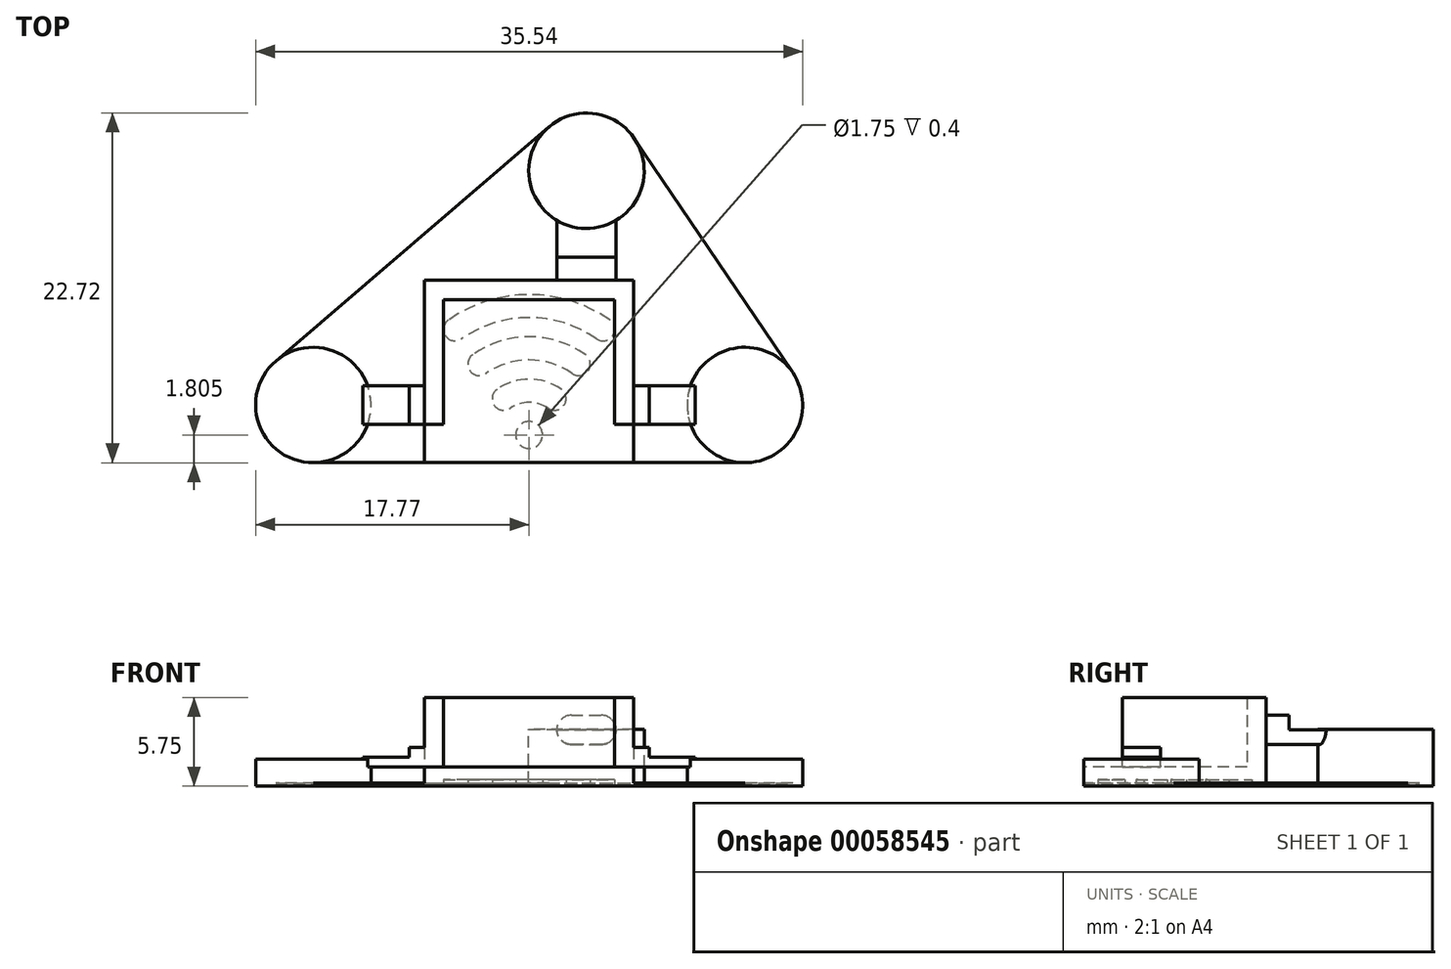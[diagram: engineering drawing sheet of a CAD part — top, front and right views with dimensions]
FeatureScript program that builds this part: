
annotation { "Feature Type Name" : "Feature", "Feature Type Description" : "" }
export const myFeature = defineFeature(function(context is Context, id is Id, definition is map)
    precondition{}
    {
        {
            var Q0;
            Q0=qCreatedBy(makeId("Top.planeOp"),FACE);
            var sketch = newSketch(context, id + "F0", { "sketchPlane" : qUnion([Q0])});
            skLineSegment(sketch, "E0.bottom", {"start": v(-6.8, 5.93) * mm, "end": v(6.8, 5.92) * mm});
            skLineSegment(sketch, "E0.top", {"start": v(-6.8, -5.92) * mm, "end": v(6.8, -5.93) * mm});
            skLineSegment(sketch, "E0.left", {"start": v(-6.8, 5.93) * mm, "end": v(-6.8, -5.93) * mm});
            skLineSegment(sketch, "E0.right", {"start": v(6.8, 5.93) * mm, "end": v(6.8, -5.93) * mm});
            skLineSegment(sketch, "E1", {"start": v(0, 11.13) * mm, "end": v(0, -11.32) * mm, "construction": true});
            skLineSegment(sketch, "E2", {"start": v(-11.98, 0) * mm, "end": v(11.2, 0) * mm, "construction": true});
            skSolve(sketch);
        }
        {
            var Q0;
            Q0 = qSketchRegion(id + "F0", true);
            extrude(context, id + "F1", {"entities" : qUnion([Q0]), "depth" : 5.75 * mm});
        }
        {
            var Q0;
            Q0=makeQuery(id+"F1.opExtrude","CAP_FACE",FACE,{"disambiguationData":[OSD([sQuery(id+"F0.wireOp",EDGE,"E0.bottom"),sQuery(id+"F0.wireOp",EDGE,"E0.top"),sQuery(id+"F0.wireOp",EDGE,"E0.left"),sQuery(id+"F0.wireOp",EDGE,"E0.right")])],"isStart":false});
            shell(context, id + "F2", {"entities" : qUnion([Q0]), "thickness" : 1.25 * mm});
        }
        {
            var Q0;
            Q0=makeQuery(id+"F1.opExtrude","SWEPT_FACE",FACE,{"disambiguationData":[OSD([sQuery(id+"F0.wireOp",EDGE,"E0.right")])]});
            var sketch = newSketch(context, id + "F3", { "sketchPlane" : qUnion([Q0])});
            skLineSegment(sketch, "E3.bottom", {"start": v(-0.93, 2.5) * mm, "end": v(-3.43, 2.5) * mm});
            skLineSegment(sketch, "E3.top", {"start": v(-0.93, 1.25) * mm, "end": v(-3.43, 1.25) * mm});
            skLineSegment(sketch, "E3.left", {"start": v(-0.93, 2.5) * mm, "end": v(-0.93, 1.25) * mm});
            skLineSegment(sketch, "E4", {"start": v(-3.43, 1.25) * mm, "end": v(-3.43, 2.5) * mm});
            skSolve(sketch);
        }
        {
            var Q0;
            Q0 = qSketchRegion(id + "F3", true);
            extrude(context, id + "F4", {"entities" : qUnion([Q0]), "operationType" : NewBodyOperationType.ADD, "depth" : 1 * mm});
        }
        {
            var Q0;
            Q0=makeQuery(id+"F1.opExtrude","SWEPT_BODY",BODY,{"disambiguationData":[OSD([sQuery(id+"F0.wireOp",EDGE,"E0.bottom"),sQuery(id+"F0.wireOp",EDGE,"E0.top"),sQuery(id+"F0.wireOp",EDGE,"E0.left"),sQuery(id+"F0.wireOp",EDGE,"E0.right")])]});
            var Q1;
            Q1=qCreatedBy(makeId("Right.planeOp"),FACE);
            mirror(context, id + "F5", {"operationType" : NewBodyOperationType.ADD, "entities" : qUnion([Q0]), "mirrorPlane" : qUnion([Q1])});
        }
        {
            var Q0;
            {var subQ0=makeQuery(id+"F4.boolean.opBoolean","MERGE",FACE,{"derivedFrom":[makeQuery(id+"F1.opExtrude","SWEPT_FACE",FACE,{"disambiguationData":[OSD([sQuery(id+"F0.wireOp",EDGE,"E0.top")])]}),makeQuery(id+"F4.opExtrude","SWEPT_FACE",FACE,{"disambiguationData":[OSD([sQuery(id+"F3.wireOp",EDGE,"E3.right")])]})]});Q0=makeQuery(id+"F5.boolean.opBoolean","MERGE",FACE,{"derivedFrom":[subQ0,makeQuery(id+"F5.opPattern","COPY",FACE,{"derivedFrom":subQ0,"instanceName":"1"})]});}
            var sketch = newSketch(context, id + "F6", { "sketchPlane" : qUnion([Q0])});
            skLineSegment(sketch, "E5.bottom", {"start": v(-2.5, 3.65) * mm, "end": v(2.5, 3.65) * mm});
            skLineSegment(sketch, "E5.top", {"start": v(-2.5, 2.5) * mm, "end": v(2.5, 2.5) * mm});
            skLineSegment(sketch, "E5.left", {"start": v(-2.5, 3.65) * mm, "end": v(-2.5, 2.5) * mm});
            skLineSegment(sketch, "E5.right", {"start": v(2.5, 3.65) * mm, "end": v(2.5, 2.5) * mm});
            skSolve(sketch);
        }
        {
            var Q0;
            Q0 = qSketchRegion(id + "F6", true);
            extrude(context, id + "F7", {"entities" : qUnion([Q0]), "operationType" : NewBodyOperationType.ADD, "depth" : 1.5 * mm});
        }
        {
            var Q0;
            Q0=makeQuery(id+"F1.opExtrude","SWEPT_FACE",FACE,{"disambiguationData":[OSD([sQuery(id+"F0.wireOp",EDGE,"E0.bottom")])]});
            var sketch = newSketch(context, id + "F8", { "sketchPlane" : qUnion([Q0])});
            skLineSegment(sketch, "E6.bottom", {"start": v(-2.75, 2.7) * mm, "end": v(-4.7, 2.7) * mm});
            skLineSegment(sketch, "E6.top", {"start": v(-2.75, 4.6) * mm, "end": v(-4.7, 4.6) * mm});
            skLineSegment(sketch, "E6.left", {"start": v(-1.8, 3.65) * mm, "end": v(-1.8, 3.65) * mm});
            skLineSegment(sketch, "E6.right", {"start": v(-5.65, 3.65) * mm, "end": v(-5.65, 3.65) * mm});
            skPoint(sketch, "E7.visualSharp", {"position": v(-1.8, 2.7) * mm});
            skArc(sketch, "E7.filletArc", {"start": v(-2.75, 2.7) * mm, "mid": v(-2.08, 2.98) * mm, "end": v(-1.8, 3.65) * mm});
            skPoint(sketch, "E8.visualSharp", {"position": v(-1.8, 4.6) * mm});
            skArc(sketch, "E8.filletArc", {"start": v(-1.8, 3.65) * mm, "mid": v(-2.08, 4.32) * mm, "end": v(-2.75, 4.6) * mm});
            skPoint(sketch, "E9.visualSharp", {"position": v(-5.65, 4.6) * mm});
            skArc(sketch, "E9.filletArc", {"start": v(-4.7, 4.6) * mm, "mid": v(-5.37, 4.32) * mm, "end": v(-5.65, 3.65) * mm});
            skPoint(sketch, "E10.visualSharp", {"position": v(-5.65, 2.7) * mm});
            skArc(sketch, "E10.filletArc", {"start": v(-5.65, 3.65) * mm, "mid": v(-5.37, 2.98) * mm, "end": v(-4.7, 2.7) * mm});
            skSolve(sketch);
        }
        {
            var Q0;
            Q0 = qSketchRegion(id + "F8", true);
            extrude(context, id + "F9", {"entities" : qUnion([Q0]), "operationType" : NewBodyOperationType.ADD, "depth" : 1.5 * mm});
        }
        {
            var Q0;
            Q0=qCreatedBy(makeId("Right.planeOp"),FACE);
            var sketch = newSketch(context, id + "F10", { "sketchPlane" : qUnion([Q0])});
            skLineSegment(sketch, "E11.bottom", {"start": v(-3.43, 1.25) * mm, "end": v(-7.79, 1.25) * mm});
            skLineSegment(sketch, "E11.top", {"start": v(-3.43, 5.94) * mm, "end": v(-7.79, 5.94) * mm});
            skLineSegment(sketch, "E11.left", {"start": v(-3.43, 1.25) * mm, "end": v(-3.43, 5.94) * mm});
            skLineSegment(sketch, "E11.right", {"start": v(-7.79, 1.25) * mm, "end": v(-7.79, 5.94) * mm});
            skSolve(sketch);
        }
        {
            var Q0;
            Q0 = qSketchRegion(id + "F10", true);
            extrude(context, id + "F11", {"entities" : qUnion([Q0]), "operationType" : NewBodyOperationType.REMOVE, "endBound" : BoundingType.THROUGH_ALL, "oppositeDirection" : true, "depth" : 25 * mm, "hasSecondDirection" : true, "secondDirectionBound" : SecondDirectionBoundingType.THROUGH_ALL, "secondDirectionOppositeDirection" : false, "secondDirectionDepth" : 25 * mm});
        }
        {
            var Q0;
            Q0=qCreatedBy(makeId("Top.planeOp"),FACE);
            var sketch = newSketch(context, id + "F12", { "sketchPlane" : qUnion([Q0])});
            skCircle(sketch, "E12", {"center": v(0, -4.12) * mm, "radius": 0.88 * mm});
            skLineSegment(sketch, "E13", {"start": v(0, 4.9) * mm, "end": v(0, -4.12) * mm, "construction": true});
            skLineSegment(sketch, "E14", {"start": v(0, -4.12) * mm, "end": v(-5.13, 3.2) * mm, "construction": true});
            skLineSegment(sketch, "E15", {"start": v(0, -4.12) * mm, "end": v(5.18, 3.28) * mm, "construction": true});
            skArc(sketch, "E16", {"start": v(1.65, -1.77) * mm, "mid": v(0, -1.25) * mm, "end": v(-1.65, -1.77) * mm});
            skArc(sketch, "E17", {"start": v(3.23, 0.48) * mm, "mid": v(0, 1.5) * mm, "end": v(-3.23, 0.48) * mm});
            skArc(sketch, "E18", {"start": v(4.8, 2.74) * mm, "mid": v(0, 4.25) * mm, "end": v(-4.8, 2.74) * mm});
            skArc(sketch, "E19.0.startCap", {"start": v(5.23, 3.35) * mm, "mid": v(5.42, 2.3) * mm, "end": v(4.37, 2.12) * mm});
            skArc(sketch, "E19.0.endCap", {"start": v(-4.37, 2.12) * mm, "mid": v(-5.42, 2.3) * mm, "end": v(-5.23, 3.35) * mm});
            skArc(sketch, "E19.0.left", {"start": v(4.37, 2.12) * mm, "mid": v(0, 3.5) * mm, "end": v(-4.37, 2.12) * mm});
            skArc(sketch, "E19.0.right", {"start": v(5.23, 3.35) * mm, "mid": v(0, 5) * mm, "end": v(-5.23, 3.35) * mm});
            skArc(sketch, "E19.1.startCap", {"start": v(3.66, 1.1) * mm, "mid": v(3.84, 0.05) * mm, "end": v(2.8, -0.13) * mm});
            skArc(sketch, "E19.1.endCap", {"start": v(-2.8, -0.13) * mm, "mid": v(-3.84, 0.05) * mm, "end": v(-3.66, 1.1) * mm});
            skArc(sketch, "E19.1.left", {"start": v(2.8, -0.13) * mm, "mid": v(0, 0.75) * mm, "end": v(-2.8, -0.13) * mm});
            skArc(sketch, "E19.1.right", {"start": v(3.66, 1.1) * mm, "mid": v(0, 2.25) * mm, "end": v(-3.66, 1.1) * mm});
            skArc(sketch, "E19.2.startCap", {"start": v(2.08, -1.16) * mm, "mid": v(2.26, -2.2) * mm, "end": v(1.22, -2.38) * mm});
            skArc(sketch, "E19.2.endCap", {"start": v(-1.22, -2.38) * mm, "mid": v(-2.26, -2.2) * mm, "end": v(-2.08, -1.16) * mm});
            skArc(sketch, "E19.2.left", {"start": v(1.22, -2.38) * mm, "mid": v(0, -2) * mm, "end": v(-1.22, -2.38) * mm});
            skArc(sketch, "E19.2.right", {"start": v(2.08, -1.16) * mm, "mid": v(0, -0.5) * mm, "end": v(-2.08, -1.16) * mm});
            skSolve(sketch);
        }
        {
            var Q0;
            Q0=makeQuery(id+"F4.opExtrude","CAP_FACE",FACE,{"disambiguationData":[OSD([sQuery(id+"F3.wireOp",EDGE,"E3.bottom"),sQuery(id+"F3.wireOp",EDGE,"E3.top"),sQuery(id+"F3.wireOp",EDGE,"E3.left"),sQuery(id+"F3.wireOp",EDGE,"E4")])],"isStart":false});
            var sketch = newSketch(context, id + "F13", { "sketchPlane" : qUnion([Q0])});
            skLineSegment(sketch, "E20.bottom", {"start": v(-0.93, 1.25) * mm, "end": v(-3.43, 1.25) * mm});
            skLineSegment(sketch, "E20.top", {"start": v(-0.93, 1.88) * mm, "end": v(-3.43, 1.88) * mm});
            skLineSegment(sketch, "E20.left", {"start": v(-0.93, 1.25) * mm, "end": v(-0.93, 1.88) * mm});
            skLineSegment(sketch, "E20.right", {"start": v(-3.43, 1.25) * mm, "end": v(-3.43, 1.88) * mm});
            skSolve(sketch);
        }
        {
            var Q0;
            Q0 = qSketchRegion(id + "F13", true);
            extrude(context, id + "F14", {"entities" : qUnion([Q0]), "operationType" : NewBodyOperationType.ADD, "depth" : 3 * mm});
        }
        {
            var Q0;
            Q0=makeQuery(id+"F5.opPattern","COPY",FACE,{"derivedFrom":makeQuery(id+"F4.opExtrude","CAP_FACE",FACE,{"disambiguationData":[OSD([sQuery(id+"F3.wireOp",EDGE,"E3.bottom"),sQuery(id+"F3.wireOp",EDGE,"E3.top"),sQuery(id+"F3.wireOp",EDGE,"E3.left"),sQuery(id+"F3.wireOp",EDGE,"E4")])],"isStart":false}),"instanceName":"1"});
            var sketch = newSketch(context, id + "F15", { "sketchPlane" : qUnion([Q0])});
            skLineSegment(sketch, "E21.bottom", {"start": v(0.93, 1.25) * mm, "end": v(3.43, 1.25) * mm});
            skLineSegment(sketch, "E21.top", {"start": v(0.93, 1.88) * mm, "end": v(3.43, 1.88) * mm});
            skLineSegment(sketch, "E21.left", {"start": v(0.93, 1.25) * mm, "end": v(0.93, 1.88) * mm});
            skLineSegment(sketch, "E21.right", {"start": v(3.43, 1.25) * mm, "end": v(3.43, 1.88) * mm});
            skSolve(sketch);
        }
        {
            var Q0;
            Q0 = qSketchRegion(id + "F15", true);
            extrude(context, id + "F16", {"entities" : qUnion([Q0]), "operationType" : NewBodyOperationType.ADD, "depth" : 3 * mm});
        }
        {
            var Q0;
            Q0=makeQuery(id+"F9.opExtrude","CAP_FACE",FACE,{"disambiguationData":[OSD([sQuery(id+"F8.wireOp",EDGE,"E6.bottom"),sQuery(id+"F8.wireOp",EDGE,"E6.top"),sQuery(id+"F8.wireOp",EDGE,"E7.filletArc"),sQuery(id+"F8.wireOp",EDGE,"E8.filletArc"),sQuery(id+"F8.wireOp",EDGE,"E9.filletArc"),sQuery(id+"F8.wireOp",EDGE,"E10.filletArc")])],"isStart":false});
            var sketch = newSketch(context, id + "F17", { "sketchPlane" : qUnion([Q0])});
            skArc(sketch, "E22.0", {"start": v(-2.75, 2.7) * mm, "mid": v(-2.08, 2.98) * mm, "end": v(-1.8, 3.65) * mm});
            skLineSegment(sketch, "E22.1", {"start": v(-2.75, 2.7) * mm, "end": v(-4.7, 2.7) * mm});
            skArc(sketch, "E22.2", {"start": v(-5.65, 3.65) * mm, "mid": v(-5.37, 2.98) * mm, "end": v(-4.7, 2.7) * mm});
            skLineSegment(sketch, "E23", {"start": v(-1.8, 3.65) * mm, "end": v(-5.65, 3.65) * mm});
            skSolve(sketch);
        }
        {
            var Q0;
            Q0=makeQuery(id+"F17.imprint","IMPRINT",FACE,{"disambiguationData":[TD([[makeQuery(id+"F17.imprint","IMPRINT",EDGE,{"derivedFrom":sQuery(id+"F17.wireOp",EDGE,"E22.0")}),1.0]])]});
            extrude(context, id + "F18", {"entities" : qUnion([Q0]), "operationType" : NewBodyOperationType.ADD, "depth" : 3 * mm});
        }
        {
            var Q0;
            Q0=makeQuery(id+"F16.boolean.opBoolean","MERGE",FACE,{"derivedFrom":[makeQuery(id+"F5.opPattern","COPY",FACE,{"derivedFrom":makeQuery(id+"F4.opExtrude","SWEPT_FACE",FACE,{"disambiguationData":[OSD([sQuery(id+"F3.wireOp",EDGE,"E3.top")])]}),"instanceName":"1"}),makeQuery(id+"F16.opExtrude","SWEPT_FACE",FACE,{"disambiguationData":[OSD([sQuery(id+"F15.wireOp",EDGE,"E21.bottom")])]})]});
            var sketch = newSketch(context, id + "F19", { "sketchPlane" : qUnion([Q0])});
            skCircle(sketch, "E24", {"center": v(-14.02, 2.18) * mm, "radius": 3.75 * mm});
            skCircle(sketch, "E25.MirrorC", {"center": v(14.02, 2.18) * mm, "radius": 3.75 * mm});
            skLineSegment(sketch, "E26", {"start": v(-10.8, 2.18) * mm, "end": v(10.81, 2.17) * mm, "construction": true});
            skSolve(sketch);
        }
        {
            var Q0;
            Q0 = qSketchRegion(id + "F19", true);
            var Q1;
            Q1=qCreatedBy(makeId("Top.planeOp"),FACE);
            extrude(context, id + "F20", {"entities" : qUnion([Q0]), "operationType" : NewBodyOperationType.ADD, "endBound" : BoundingType.UP_TO_SURFACE, "endBoundEntityFace" : qUnion([Q1]), "depth" : 25 * mm, "hasSecondDirection" : true, "secondDirectionOppositeDirection" : true, "secondDirectionDepth" : .5 * mm});
        }
        {
            var Q0;
            Q0=makeQuery(id+"F18.boolean.opBoolean","MERGE",FACE,{"derivedFrom":[makeQuery(id+"F9.opExtrude","SWEPT_FACE",FACE,{"disambiguationData":[OSD([sQuery(id+"F8.wireOp",EDGE,"E6.bottom")])]}),makeQuery(id+"F18.opExtrude","SWEPT_FACE",FACE,{"disambiguationData":[OSD([sQuery(id+"F17.wireOp",EDGE,"E22.1")])]})]});
            var sketch = newSketch(context, id + "F21", { "sketchPlane" : qUnion([Q0])});
            skCircle(sketch, "E27", {"center": v(3.73, -13.04) * mm, "radius": 3.75 * mm});
            skPoint(sketch, "E28", {"position": v(3.73, -10.43) * mm});
            skSolve(sketch);
        }
        {
            var Q0;
            Q0 = qSketchRegion(id + "F21", true);
            var Q1;
            Q1=qCreatedBy(makeId("Top.planeOp"),FACE);
            extrude(context, id + "F22", {"entities" : qUnion([Q0]), "operationType" : NewBodyOperationType.ADD, "endBound" : BoundingType.UP_TO_SURFACE, "endBoundEntityFace" : qUnion([Q1]), "depth" : 25 * mm, "hasSecondDirection" : true, "secondDirectionOppositeDirection" : true, "secondDirectionDepth" : 1 * mm});
        }
        {
            var Q0;
            Q0=qCreatedBy(makeId("Top.planeOp"),FACE);
            var sketch = newSketch(context, id + "F23", { "sketchPlane" : qUnion([Q0])});
            skArc(sketch, "E29.0.0", {"start": v(-16.46, 0.67) * mm, "mid": v(-17.54, -3.48) * mm, "end": v(-14.02, -5.92) * mm});
            skArc(sketch, "E29.1.0", {"start": v(14.02, -5.92) * mm, "mid": v(17.33, -3.93) * mm, "end": v(17.13, -0.07) * mm});
            skArc(sketch, "E29.2.0", {"start": v(6.83, 15.14) * mm, "mid": v(4.22, 16.76) * mm, "end": v(1.28, 15.9) * mm});
            skLineSegment(sketch, "E30", {"start": v(-14.02, -5.92) * mm, "end": v(14.02, -5.92) * mm});
            skLineSegment(sketch, "E31", {"start": v(-16.46, 0.67) * mm, "end": v(1.28, 15.9) * mm});
            skLineSegment(sketch, "E32", {"start": v(6.83, 15.14) * mm, "end": v(17.13, -0.07) * mm});
            skSolve(sketch);
        }
        {
            var Q0;
            Q0 = qSketchRegion(id + "F23", true);
            extrude(context, id + "F24", {"entities" : qUnion([Q0]), "operationType" : NewBodyOperationType.ADD, "depth" : .2 * mm});
        }
        {
            var Q0;
            Q0 = qSketchRegion(id + "F12", true);
            extrude(context, id + "F25", {"entities" : qUnion([Q0]), "operationType" : NewBodyOperationType.REMOVE, "depth" : .4 * mm});
        }
    });
